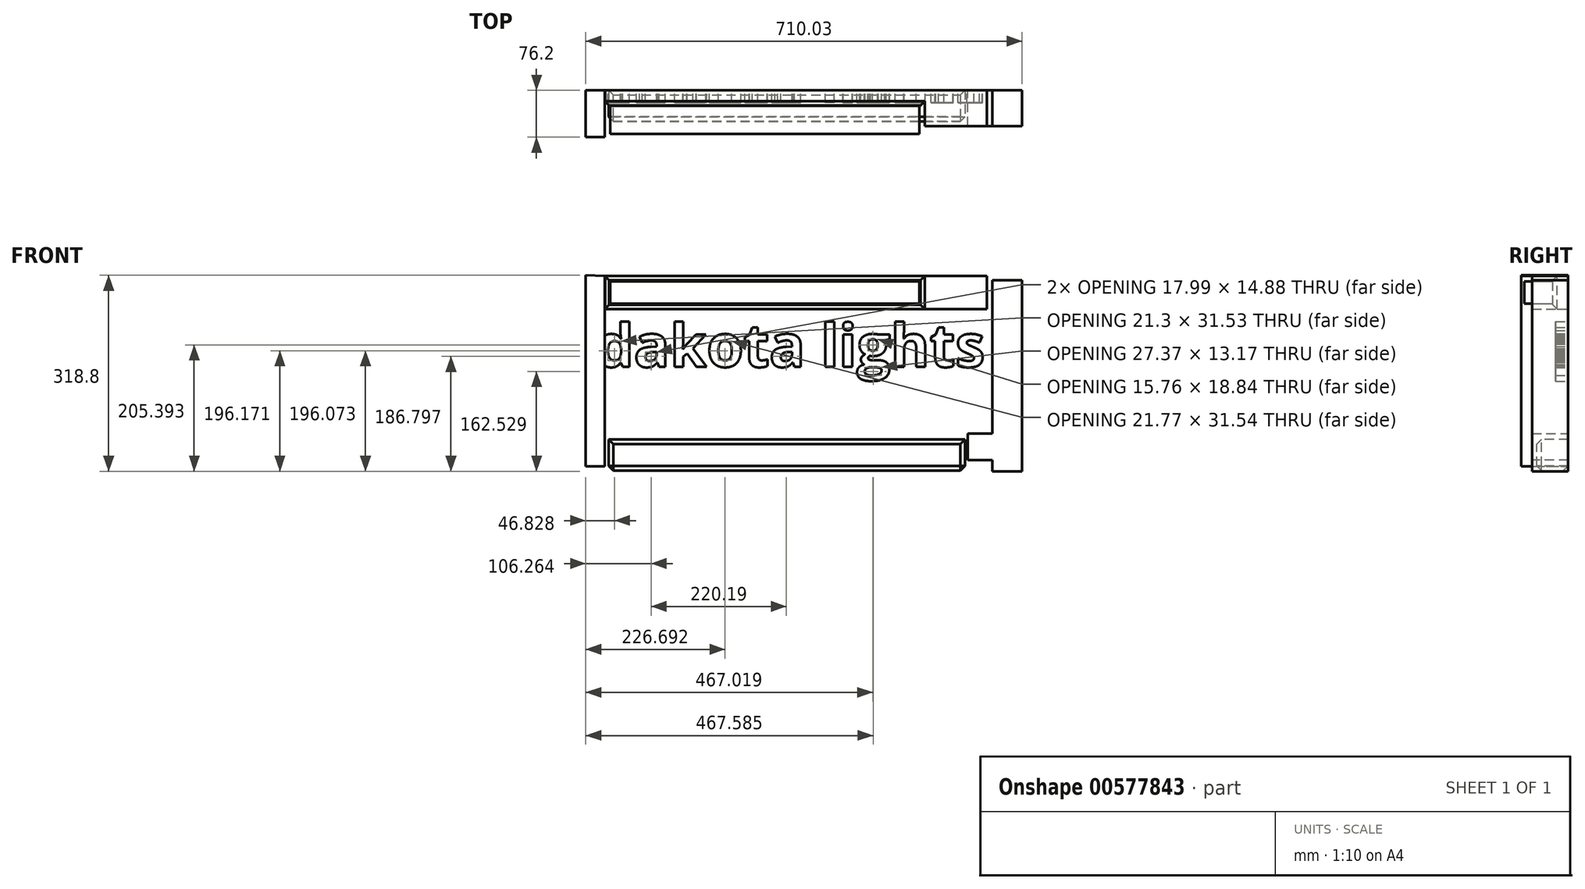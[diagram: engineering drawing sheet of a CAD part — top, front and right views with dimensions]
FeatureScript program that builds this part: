
annotation { "Feature Type Name" : "Feature", "Feature Type Description" : "" }
export const myFeature = defineFeature(function(context is Context, id is Id, definition is map)
    precondition{}
    {
        {
            var Q0;
            Q0=qCreatedBy(makeId("Front.planeOp"),FACE);
            var sketch = newSketch(context, id + "F0", { "sketchPlane" : qUnion([Q0])});
            skText(sketch, "E0", { "text": "dakota lights", "fontName": "OpenSans-Bold.ttf"});
            const initialGuessF0  = {"E0": [-0.06138, -0.03483, 1, 0, 0.06961]};
            skSetInitialGuess(sketch, initialGuessF0);
            skSolve(sketch);
        }
        {
            var Q0;
            Q0 = qSketchRegion(id + "F0", true);
            extrude(context, id + "F1", {"entities" : qUnion([Q0]), "depth" : 20.32 * mm, "offsetDistance" : 25.4 * mm});
        }
        {
            var Q0;
            Q0=qCreatedBy(makeId("Front.planeOp"),FACE);
            var sketch = newSketch(context, id + "F2", { "sketchPlane" : qUnion([Q0])});
            skLineSegment(sketch, "E1.bottom", {"start": v(-47.35, 113.31) * mm, "end": v(472.85, 113.31) * mm});
            skLineSegment(sketch, "E1.top", {"start": v(-47.35, 59.28) * mm, "end": v(472.85, 59.28) * mm});
            skLineSegment(sketch, "E1.left", {"start": v(-47.35, 113.31) * mm, "end": v(-47.35, 59.28) * mm});
            skLineSegment(sketch, "E1.right", {"start": v(472.85, 113.31) * mm, "end": v(472.85, 59.28) * mm});
            skPoint(sketch, "E1.middle", {"position": v(212.75, 86.3) * mm});
            skSolve(sketch);
        }
        {
            var Q0;
            Q0 = qSketchRegion(id + "F2", true);
            extrude(context, id + "F3", {"entities" : qUnion([Q0]), "depth" : 25.4 * mm, "offsetDistance" : 25.4 * mm});
        }
        {
            var Q0;
            Q0=makeQuery(id+"F3.opExtrude","CAP_FACE",FACE,{"disambiguationData":[OSD([sQuery(id+"F2.wireOp",EDGE,"E1.bottom"),sQuery(id+"F2.wireOp",EDGE,"E1.top"),sQuery(id+"F2.wireOp",EDGE,"E1.left"),sQuery(id+"F2.wireOp",EDGE,"E1.right")])],"isStart":false});
            chamfer(context, id + "F4", {"entities" : qUnion([Q0]), "width" : 7.62 * mm, "tangentPropagation" : true});
        }
        {
            var Q0;
            Q0=makeQuery(id+"F3.opExtrude","SWEPT_FACE",FACE,{"disambiguationData":[OSD([sQuery(id+"F2.wireOp",EDGE,"E1.right")])]});
            extrude(context, id + "F5", {"entities" : qUnion([Q0]), "operationType" : NewBodyOperationType.ADD, "depth" : 100.93 * mm, "offsetDistance" : 25.4 * mm});
        }
        {
            var Q0;
            Q0=qCreatedBy(makeId("Front.planeOp"),FACE);
            var sketch = newSketch(context, id + "F6", { "sketchPlane" : qUnion([Q0])});
            skLineSegment(sketch, "E2", {"start": v(-41.43, -152.77) * mm, "end": v(538.5, -152.77) * mm});
            skSolve(sketch);
        }
        {
            var Q0;
            Q0=sQuery(id+"F6.wireOp",EDGE,"E2");
            extrude(context, id + "F7", {"bodyType" : ToolBodyType.SURFACE, "surfaceEntities" : qUnion([Q0]), "depth" : 50.8 * mm, "offsetDistance" : 25.4 * mm});
        }
        {
            var Q0;
            Q0=makeQuery(id+"F7.opExtrude","SWEPT_FACE",FACE,{"disambiguationData":[OSD([sQuery(id+"F6.wireOp",EDGE,"E2")])]});
            extrude(context, id + "F8", {"entities" : qUnion([Q0]), "depth" : 50.8 * mm, "offsetDistance" : 25.4 * mm});
        }
        {
            var Q0;
            Q0=makeQuery(id+"F8.opExtrude","CAP_FACE",FACE,{"disambiguationData":[OSD([sQuery(id+"F6.wireOp",EDGE,"E2")])],"isStart":false});
            var Q1;
            {var subQ0=sQuery(id+"F6.wireOp",EDGE,"E2");Q1=makeQuery(id+"F8.opExtrude","SWEPT_FACE",FACE,{"disambiguationData":[OSD([subQ0]),TDD([makeQuery(id+"F7.opExtrude","CAP_EDGE",EDGE,{"disambiguationData":[OSD([subQ0])],"isStart":false})])]});}
            chamfer(context, id + "F9", {"entities" : qUnion([Q0, Q1]), "width" : 7.62 * mm});
        }
        {
            var Q0;
            Q0=makeQuery(id+"F3.opExtrude","CAP_FACE",FACE,{"disambiguationData":[OSD([sQuery(id+"F2.wireOp",EDGE,"E1.bottom"),sQuery(id+"F2.wireOp",EDGE,"E1.top"),sQuery(id+"F2.wireOp",EDGE,"E1.left"),sQuery(id+"F2.wireOp",EDGE,"E1.right")])],"isStart":false});
            chamfer(context, id + "F10", {"entities" : qUnion([Q0]), "width" : 2.54 * mm, "tangentPropagation" : true});
        }
        {
            var Q0;
            Q0=qCreatedBy(makeId("Front.planeOp"),FACE);
            var sketch = newSketch(context, id + "F11", { "sketchPlane" : qUnion([Q0])});
            skLineSegment(sketch, "E3", {"start": v(-47.6, 113.4) * mm, "end": v(-47.6, -196.35) * mm});
            skLineSegment(sketch, "E4", {"start": v(-47.6, -196.35) * mm, "end": v(-78.63, -196.35) * mm});
            skLineSegment(sketch, "E5", {"start": v(-78.63, -196.35) * mm, "end": v(-78.63, 114.19) * mm});
            skLineSegment(sketch, "E6", {"start": v(-78.63, 114.19) * mm, "end": v(-47.6, 113.4) * mm});
            skSolve(sketch);
        }
        {
            var Q0;
            Q0=makeQuery(id+"F11.imprint","IMPRINT",FACE,{"disambiguationData":[TD([[makeQuery(id+"F11.imprint","IMPRINT",EDGE,{"derivedFrom":sQuery(id+"F11.wireOp",EDGE,"E3")}),-1.0]])]});
            extrude(context, id + "F12", {"entities" : qUnion([Q0]), "operationType" : NewBodyOperationType.ADD, "depth" : 30.48 * mm, "offsetDistance" : 25.4 * mm});
        }
        {
            var Q0;
            Q0=qCreatedBy(makeId("Front.planeOp"),FACE);
            var sketch = newSketch(context, id + "F13", { "sketchPlane" : qUnion([Q0])});
            skLineSegment(sketch, "E7", {"start": v(582.76, 106.15) * mm, "end": v(582.76, -204.61) * mm});
            skLineSegment(sketch, "E8", {"start": v(582.76, -204.61) * mm, "end": v(631.4, -204.61) * mm});
            skLineSegment(sketch, "E9", {"start": v(631.4, -204.61) * mm, "end": v(631.4, 106.11) * mm});
            skLineSegment(sketch, "E10", {"start": v(631.4, 106.11) * mm, "end": v(582.76, 106.15) * mm});
            skSolve(sketch);
        }
        {
            var Q0;
            Q0=makeQuery(id+"F13.imprint","IMPRINT",FACE,{"disambiguationData":[TD([[makeQuery(id+"F13.imprint","IMPRINT",EDGE,{"derivedFrom":sQuery(id+"F13.wireOp",EDGE,"E7")}),1.0]])]});
            extrude(context, id + "F14", {"entities" : qUnion([Q0]), "depth" : 25.4 * mm, "offsetDistance" : 25.4 * mm});
        }
        {
            var Q0;
            Q0=qCreatedBy(makeId("Front.planeOp"),FACE);
            var sketch = newSketch(context, id + "F15", { "sketchPlane" : qUnion([Q0])});
            skLineSegment(sketch, "E11", {"start": v(586.22, -143.52) * mm, "end": v(542.63, -143.52) * mm});
            skLineSegment(sketch, "E12", {"start": v(542.63, -143.52) * mm, "end": v(542.63, -186.33) * mm});
            skLineSegment(sketch, "E13", {"start": v(542.63, -186.33) * mm, "end": v(586.22, -186.33) * mm});
            skLineSegment(sketch, "E14", {"start": v(586.22, -186.33) * mm, "end": v(586.22, -143.52) * mm});
            skSolve(sketch);
        }
        {
            var Q0;
            Q0=makeQuery(id+"F15.imprint","IMPRINT",FACE,{"disambiguationData":[TD([[makeQuery(id+"F15.imprint","IMPRINT",EDGE,{"derivedFrom":sQuery(id+"F15.wireOp",EDGE,"E11")}),1.0]])]});
            extrude(context, id + "F16", {"entities" : qUnion([Q0]), "operationType" : NewBodyOperationType.ADD, "depth" : 25.4 * mm, "offsetDistance" : 25.4 * mm});
        }
        {
            var Q0;
            Q0=makeQuery(id+"F16.boolean.opBoolean","MERGE",FACE,{"derivedFrom":[makeQuery(id+"F14.opExtrude","CAP_FACE",FACE,{"disambiguationData":[OSD([sQuery(id+"F13.wireOp",EDGE,"E7"),sQuery(id+"F13.wireOp",EDGE,"E8"),sQuery(id+"F13.wireOp",EDGE,"E9"),sQuery(id+"F13.wireOp",EDGE,"E10")])],"isStart":false}),makeQuery(id+"F16.opExtrude","CAP_FACE",FACE,{"disambiguationData":[OSD([sQuery(id+"F15.wireOp",EDGE,"E11"),sQuery(id+"F15.wireOp",EDGE,"E12"),sQuery(id+"F15.wireOp",EDGE,"E13"),sQuery(id+"F15.wireOp",EDGE,"E14")])],"isStart":false})]});
            extrude(context, id + "F17", {"entities" : qUnion([Q0]), "operationType" : NewBodyOperationType.ADD, "depth" : 33.02 * mm, "offsetDistance" : 25.4 * mm});
        }
        {
            var Q0;
            {var subQ0=sQuery(id+"F2.wireOp",EDGE,"E1.right");Q0=makeQuery(id+"F5.opExtrude","SWEPT_FACE",FACE,{"disambiguationData":[OSD([subQ0]),TDD([makeQuery(id+"F4.opChamfer","BLEND_EDGE",EDGE,{"blendedFrom":[makeQuery(id+"F3.opExtrude","CAP_EDGE",EDGE,{"disambiguationData":[OSD([subQ0])],"isStart":false}),makeQuery(id+"F3.opExtrude","SWEPT_FACE",FACE,{"disambiguationData":[OSD([subQ0])]})],"blendedInto":[makeQuery(id+"F3.opExtrude","SWEPT_FACE",FACE,{"disambiguationData":[OSD([subQ0])]})]})])]});}
            extrude(context, id + "F18", {"entities" : qUnion([Q0]), "operationType" : NewBodyOperationType.ADD, "depth" : 40.64 * mm, "offsetDistance" : 25.4 * mm});
        }
        {
            var Q0;
            Q0=makeQuery(id+"F3.opExtrude","CAP_FACE",FACE,{"disambiguationData":[OSD([sQuery(id+"F2.wireOp",EDGE,"E1.bottom"),sQuery(id+"F2.wireOp",EDGE,"E1.top"),sQuery(id+"F2.wireOp",EDGE,"E1.left"),sQuery(id+"F2.wireOp",EDGE,"E1.right")])],"isStart":false});
            extrude(context, id + "F19", {"entities" : qUnion([Q0]), "operationType" : NewBodyOperationType.ADD, "depth" : 45.72 * mm, "offsetDistance" : 25.4 * mm});
        }
        {
            var Q0;
            Q0=makeQuery(id+"F12.opExtrude","CAP_FACE",FACE,{"disambiguationData":[OSD([sQuery(id+"F11.wireOp",EDGE,"E3"),sQuery(id+"F11.wireOp",EDGE,"E4"),sQuery(id+"F11.wireOp",EDGE,"E5"),sQuery(id+"F11.wireOp",EDGE,"E6")])],"isStart":false});
            extrude(context, id + "F20", {"entities" : qUnion([Q0]), "operationType" : NewBodyOperationType.ADD, "depth" : 45.72 * mm, "offsetDistance" : 25.4 * mm});
        }
    });
